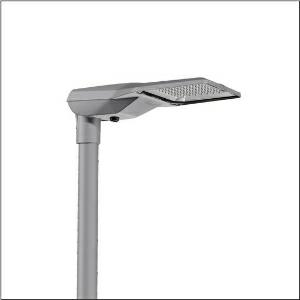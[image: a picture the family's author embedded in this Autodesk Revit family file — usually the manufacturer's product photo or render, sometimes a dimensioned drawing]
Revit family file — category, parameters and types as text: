
# Revit family: streetlight_sl_21_midi___st1_0ab_5xe3m33r08nb_1fb7
name_source: partatom
category: Lighting Fixtures
units: mm (PartAtom-declared; Revit-internal decimal feet)

## family parameters
Cut with Voids When Loaded = No
Host = Face
Light Source = No
Part Type = Normal
Room Calculation Point = No
Round Connector Dimension = Use Diameter
Shared = No

## types (1)
- --- (1 x LED, 19980 lm, 151.2 W, 3000K)
    Apparent Load = 151 VA
    CIE Flux Codes = 40 74 97 100 100
    Color Rendering = 70
    Color Temperature = 3000K
    Default Elevation = 1800 mm
    Description = Streetlight SL 21 midi, mast luminaire, primary light control with lens, of PMMA, primary optical cover: cover, of toughened safety glass, transparent, light distribution: ST1.0aB, light emission: direct distribution, primary light characteristic: asymmetric, installation type: side-entry, post-top, LED, High Power LED, rated luminous flux: 19.980lm, luminous efficacy: 132lm/W, light colour: 730, colour temperature: 3000K, control gear: D4i, control: flexible luminous flux parameterisation, time-dependent luminous flux control, constant luminous flux control, overheat protection, pre-setting: logarithmic dimming characteristic, mains connection: 230..240V, AC, 50/60Hz, start of lifetime: 151W, end of service life: 157W, reduction: 70W, luminaire housing, of diecast aluminium, powder-coated, Siteco® metallic grey (DB 702S), corrosivity category C5 mid according to DIN EN ISO 12944, please order mast flange separately, inclination adjustable: 0°, 5°, 10°, 15°, sealing non-destructively replaceable, multi-level sealing system, length: 644mm, width: 335mm, height: 110mm, mast flange for spigot size: 42mm (side-entry): 5XC10008XM4, 60/48mm (side-entry/post-top): 5XC10108XM2, 76/60mm (side-entry/post-top): 5XC10108XM1, mounting height: 4..8m, Smart Interface below, protection rating (complete): IP66, insulation class (complete): insulation class II (safety insulation), certification: CE, ENEC, ENEC+, VDE, impact resistance: IK10, permissible operating ambient temperature for outdoor applications: -40..+50°C, standard-compliant lighting for roads and squares, packaging unit: 1 piece

Light Distribution: ST1.0aB
    Height = 111 mm
    Lamp = 1 x LED
    Lamp Light Flux = 19980 lm
    Lamp Power = 151.2 W
    Lamp count = 1
    Length = 644 mm
    Luminous efficacy = 132 lm/W
    Manufacturer = Siteco
    ModVariant = No
    Model = 5XE3M33R08NB
    Number of Poles = 1
    OnlyDefault = Yes
    Power Factor = 1
    Product Name = Streetlight SL 21 midi | ST1.0aB
    Product group = mast luminaire | pylon top
    ProductGroupID = 6100
    Protection Class = Protection class II
    Protection Degree = IP 66
    RLX_Detail_Level = 1
    RLX_Emergency_Light_Flux = 0 lm
    RLX_Emergency_Type = 0
    RLX_Emergency_Type_DB = No
    RlxData = <blob elided: 26973 chars, md5=7fe30e84>
    Socket = socket
    Standby Power = 0 W
    System Light Flux = 19980 lm
    System Power = 151 W
    Type Comments = factory setting: luminous flux: 100 % | dim-lin: 254 | 802 mA
    Type Image = l_1004300.jpg
    URL = http://relux.com
    VarID = @adj_189649
    Voltage = 0 V
    Weight = 0.00 kg
    Width = 336 mm

## geometry (parser evidence)
native form markers: Blend x4, Sweep x10
no freeform markers — native parametric forms only
